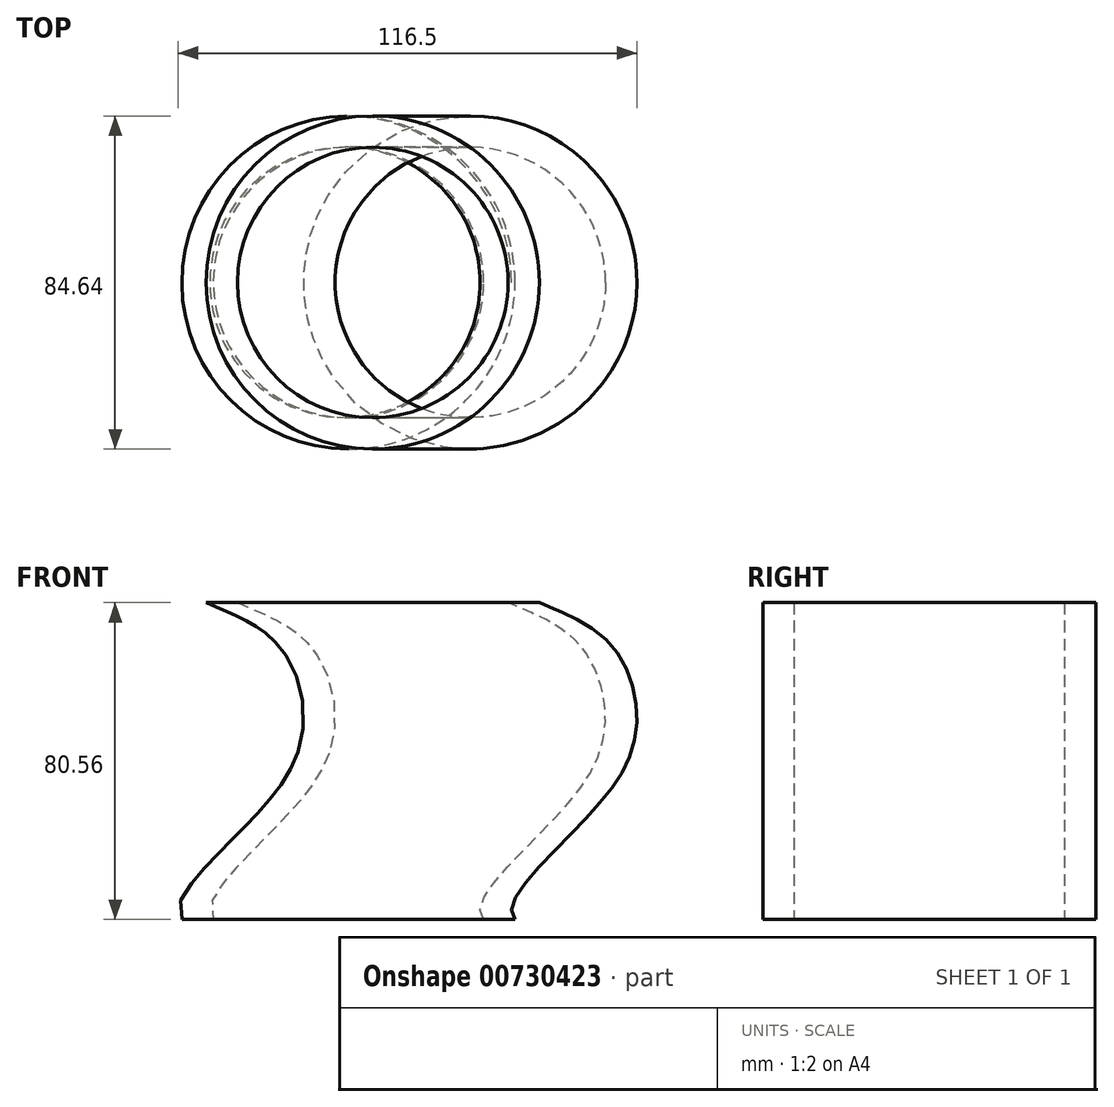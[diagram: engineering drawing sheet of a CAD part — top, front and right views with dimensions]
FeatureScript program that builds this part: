
annotation { "Feature Type Name" : "Feature", "Feature Type Description" : "" }
export const myFeature = defineFeature(function(context is Context, id is Id, definition is map)
    precondition{}
    {
        {
            var Q0;
            Q0=qCreatedBy(makeId("Top.planeOp"),FACE);
            var sketch = newSketch(context, id + "F0", { "sketchPlane" : qUnion([Q0])});
            skCircle(sketch, "E0", {"center": v(0, 0) * mm, "radius": 42.32 * mm});
            skCircle(sketch, "E1", {"center": v(0, 0) * mm, "radius": 34.35 * mm});
            skSolve(sketch);
        }
        {
            var Q0;
            Q0=qCreatedBy(makeId("Front.planeOp"),FACE);
            var sketch = newSketch(context, id + "F1", { "sketchPlane" : qUnion([Q0])});
            skFitSpline(sketch, "E2", {"points": [v(0, 0) * mm, v(12.62, 20.17) * mm, v(30.37, 45.67) * mm, v(23.46, 70.83) * mm, v(6.17, 80.56) * mm], "startDerivative": vector(-46.89, 45.84) * mm, "endDerivative": vector(-48.45, 24.75) * mm});
            skSolve(sketch);
        }
        {
            var Q0;
            Q0=makeQuery(id+"F0.imprint","IMPRINT",FACE,{"disambiguationData":[TD([[makeQuery(id+"F0.imprint","IMPRINT",EDGE,{"derivedFrom":sQuery(id+"F0.wireOp",EDGE,"E0")}),1.0]])]});
            var Q1;
            Q1=sQuery(id+"F1.wireOp",EDGE,"E2");
            sweep(context, id + "F2", {"profiles" : qUnion([Q0]), "path" : qUnion([Q1]), "keepProfileOrientation" : true});
        }
    });
